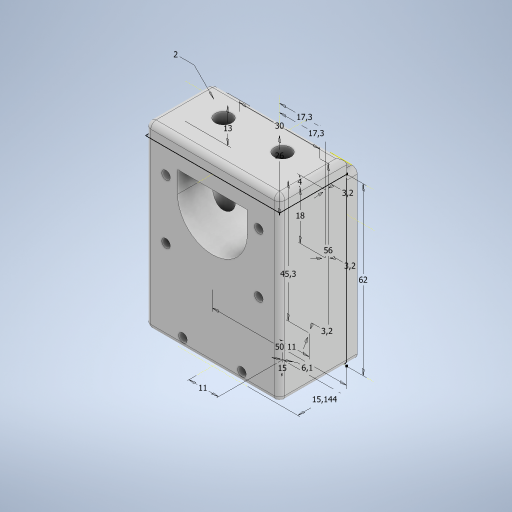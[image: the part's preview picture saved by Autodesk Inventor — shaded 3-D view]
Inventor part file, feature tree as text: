
AUTODESK INVENTOR PART (.ipt)
format: ipt  version: 2024.3 (Build 283343000, 343)  size: 376,320 bytes
history: native  units: mm
features: extrude x5, sketch x3, other x1, fillet x1, hole x1
ambient origin geometry x8: Origin, YZ Plane, XZ Plane, XY Plane, X Axis, Y Axis, Z Axis, Center Point
bodies: Body1 (feature_tree)
feature tree (11):
  other  "Bryła1"
  sketch  "Szkic1"
  extrude  "Wyciągnięcie proste1"  Depth=50.0mm
  extrude  "Wyciągnięcie proste2"  Depth=62.0mm
  sketch  "Szkic2"
  extrude  "Wyciągnięcie proste4"  Depth=13.0mm
  sketch  "Szkic3"
  extrude  "Wyciągnięcie proste6"  Depth=3.2mm
  extrude  "Wyciągnięcie proste7"  Depth=3.2mm
  fillet  "Zaokrąglenie1"  Radius=3.2mm
  hole  "Otwór1"  [1 undecoded]
note: 1 required parameter value undecoded (feature->parameter linkage not recoverable at this tier; creation-order binding heuristic only, values carry confidence <= 0.55)
